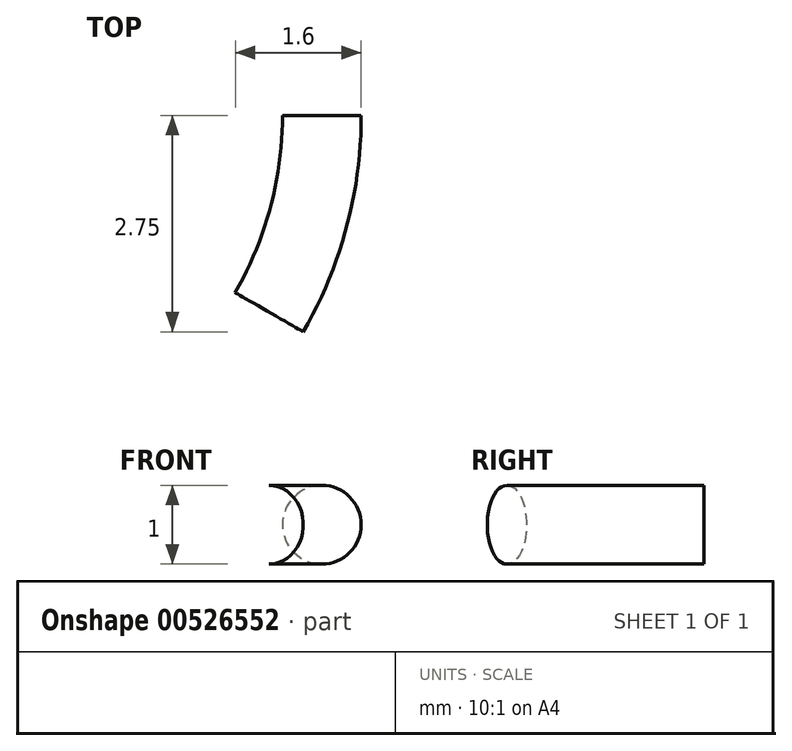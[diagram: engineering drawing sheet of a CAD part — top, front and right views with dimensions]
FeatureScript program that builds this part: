
annotation { "Feature Type Name" : "Feature", "Feature Type Description" : "" }
export const myFeature = defineFeature(function(context is Context, id is Id, definition is map)
    precondition{}
    {
        {
            var Q0;
            Q0=qCreatedBy(makeId("Front.planeOp"),FACE);
            var sketch = newSketch(context, id + "F0", { "sketchPlane" : qUnion([Q0])});
            skCircle(sketch, "E0", {"center": v(5, 0) * mm, "radius": 0.5 * mm});
            skSolve(sketch);
        }
        {
            var Q0;
            Q0=qCreatedBy(makeId("Front.planeOp"),FACE);
            var sketch = newSketch(context, id + "F1", { "sketchPlane" : qUnion([Q0])});
            skLineSegment(sketch, "E1", {"start": v(0, 9.7) * mm, "end": v(0, -6.28) * mm});
            skSolve(sketch);
        }
        {
            var Q0;
            Q0=makeQuery(id+"F0.imprint","IMPRINT",FACE,{"disambiguationData":[TD([[makeQuery(id+"F0.imprint","IMPRINT",EDGE,{"derivedFrom":sQuery(id+"F0.wireOp",EDGE,"E0")}),1.0]])]});
            var Q1;
            Q1=sQuery(id+"F1.wireOp",EDGE,"E1");
            revolve(context, id + "F2", {"entities" : qUnion([Q0]), "axis" : qUnion([Q1]), "revolveType" : RevolveType.ONE_DIRECTION, "angle" : 30 * degree});
        }
    });
